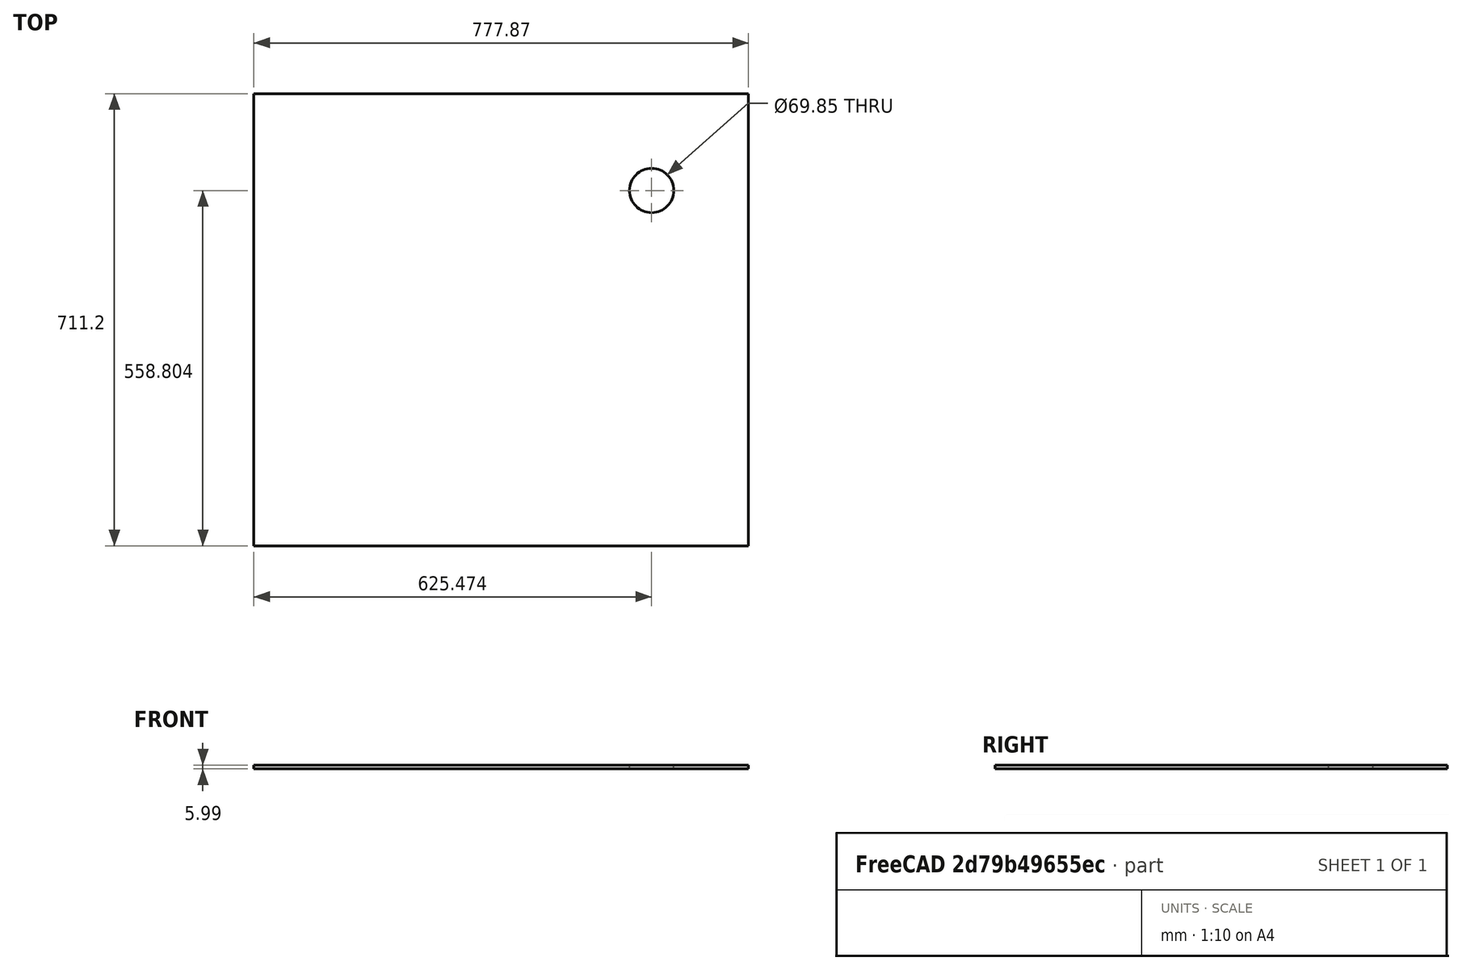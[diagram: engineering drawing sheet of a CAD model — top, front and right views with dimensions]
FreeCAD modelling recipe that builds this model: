
FCSTD DOCUMENT  (FreeCAD 0.19R24267 (Git))
Label: Inv1-P2
License: All rights reserved
LicenseURL: http://en.wikipedia.org/wiki/All_rights_reserved
objects: TechDraw::DrawViewDimension×6, TechDraw::DrawProjGroupItem×2, TechDraw::DrawHatch×2, TechDraw::DrawViewAnnotation×2, Sketcher::SketchObject×1, Part::Extrusion×1, TechDraw::DrawSVGTemplate×1, TechDraw::DrawProjGroup×1, TechDraw::DrawPage×1
note: 2 computed .brp shape members not serialized (recipe doc carries the construction recipe); baked Part::Feature solids carry a one-line shape summary decoded from their .brp

FEATURE [Sketcher::SketchObject] Sketch
  FullyConstrained = false
  sketch-geometry (5):
    g0: LineSegment StartX=-539.321 StartY=433.474 StartZ=0 EndX=238.554 EndY=433.474 EndZ=0
    g1: LineSegment StartX=238.554 StartY=433.474 StartZ=0 EndX=238.554 EndY=-277.726 EndZ=0
    g2: LineSegment StartX=238.554 StartY=-277.726 StartZ=0 EndX=-539.321 EndY=-277.726 EndZ=0
    g3: LineSegment StartX=-539.321 StartY=-277.726 StartZ=0 EndX=-539.321 EndY=433.474 EndZ=0
    g4: Circle CenterX=86.1536 CenterY=281.074 CenterZ=0 NormalX=0 NormalY=0 NormalZ=1 AngleXU=0 Radius=34.925
  constraints (13):
    c: Coincident(g0,g1)
    c: Coincident(g1,g2)
    c: Coincident(g2,g3)
    c: Coincident(g3,g0)
    c: Horizontal(g0)
    c: Horizontal(g2)
    c: Vertical(g1)
    c: Vertical(g3)
    c: DistanceY(g1,g1) = 711.2
    c: DistanceX(g0,g0) = 777.875
    c: Distance(g4,g0) = 152.4
    c: Distance(g4,g1) = 152.4
    c: Diameter(g4) = 69.85
FEATURE [Part::Extrusion] Extrude
  Base = -> Sketch
  Dir = (0,0,1)
  DirMode = 2
  FaceMakerClass = Part::FaceMakerBullseye
  LengthFwd = 5.9944
  LengthRev = 0
  Solid = true
  Symmetric = false
FEATURE [TechDraw::DrawSVGTemplate] Template
  Height = 215.9
  Orientation = 1
  Width = 279.4
FEATURE [TechDraw::DrawProjGroupItem] ProjItem  label="Front"
  CoarseView = false
  Direction = (0,0,1)
  Focus = 100
  HardHidden = false
  IsoCount = 0
  IsoHidden = false
  IsoVisible = false
  LockPosition = true
  Perspective = false
  Rotation = 0
  RotationVector = (1,0,0)
  Scale = 0.2
  ScaleType = 2
  SeamHidden = false
  SeamVisible = true
  SmoothHidden = false
  SmoothVisible = true
  Source = -> [Extrude]
  Type = 0
  X = 0
  XDirection = (1,0,0)
  Y = 0
FEATURE [TechDraw::DrawProjGroupItem] ProjItem001  label="Left"
  CoarseView = false
  Direction = (-1,0,1e-16)
  Focus = 100
  HardHidden = false
  IsoCount = 0
  IsoHidden = false
  IsoVisible = false
  LockPosition = false
  Perspective = false
  Rotation = 0
  RotationVector = (1,0,0)
  Scale = 0.2
  ScaleType = 2
  SeamHidden = false
  SeamVisible = true
  SmoothHidden = false
  SmoothVisible = true
  Source = -> [Extrude]
  Type = 1
  X = 103.584
  XDirection = (1e-16,0,1)
  Y = 0
FEATURE [TechDraw::DrawProjGroup] ProjGroup
  Anchor = -> ProjItem
  AutoDistribute = true
  LockPosition = false
  ProjectionType = 0
  Rotation = 0
  Scale = 0.2
  ScaleType = 2
  Source = -> [Extrude]
  Views = -> [ProjItem,ProjItem001]
  X = 139.7
  Y = 107.95
  spacingX = 15.0114
  spacingY = 15.0114
FEATURE [TechDraw::DrawHatch] Hatch  label="HatchF0"
  HatchPattern = <path>
  Source = -> ProjItem001 [Face0]
FEATURE [TechDraw::DrawHatch] Hatch001  label="Hatch001F0"
  HatchPattern = <path>
  Source = -> ProjItem [Face0]
FEATURE [TechDraw::DrawViewDimension] Dimension
  Arbitrary = false
  ArbitraryTolerances = false
  EqualTolerance = true
  FormatSpec = %.3f
  FormatSpecOverTolerance = %+.3f
  FormatSpecUnderTolerance = %+.3f
  Inverted = false
  LockPosition = false
  MeasureType = 1
  OverTolerance = 0
  References2D = -> [ProjItem]
  Rotation = 0
  ScaleType = 0
  TheoreticalExact = false
  Type = 1
  UnderTolerance = 0
  X = 0
  Y = -75.9014
FEATURE [TechDraw::DrawViewDimension] Dimension001
  Arbitrary = false
  ArbitraryTolerances = false
  EqualTolerance = true
  FormatSpec = %.3f
  FormatSpecOverTolerance = %+.3f
  FormatSpecUnderTolerance = %+.3f
  Inverted = false
  LockPosition = false
  MeasureType = 1
  OverTolerance = 0
  References2D = -> [ProjItem]
  Rotation = 0
  ScaleType = 0
  TheoreticalExact = false
  Type = 2
  UnderTolerance = 0
  X = 82.8238
  Y = 0
FEATURE [TechDraw::DrawViewDimension] Dimension002
  Arbitrary = false
  ArbitraryTolerances = false
  EqualTolerance = true
  FormatSpec = %.3f
  FormatSpecOverTolerance = %+.3f
  FormatSpecUnderTolerance = %+.3f
  Inverted = false
  LockPosition = false
  MeasureType = 1
  OverTolerance = 0
  References2D = -> [ProjItem001]
  Rotation = 0
  ScaleType = 0
  TheoreticalExact = false
  Type = 1
  UnderTolerance = 0
  X = 18.9749
  Y = 68.3089
FEATURE [TechDraw::DrawViewDimension] Dimension003
  Arbitrary = false
  ArbitraryTolerances = false
  EqualTolerance = true
  FormatSpec = ⌀%.3f
  FormatSpecOverTolerance = %+.3f
  FormatSpecUnderTolerance = %+.3f
  Inverted = false
  LockPosition = false
  MeasureType = 1
  OverTolerance = 0
  References2D = -> [ProjItem]
  Rotation = 0
  ScaleType = 0
  TheoreticalExact = false
  Type = 5
  UnderTolerance = 0
  X = 18.305
  Y = 22.7748
FEATURE [TechDraw::DrawViewDimension] Dimension004
  Arbitrary = false
  ArbitraryTolerances = false
  EqualTolerance = true
  FormatSpec = %.3f
  FormatSpecOverTolerance = %+.3f
  FormatSpecUnderTolerance = %+.3f
  Inverted = false
  LockPosition = false
  MeasureType = 1
  OverTolerance = 0
  References2D = -> [ProjItem]
  Rotation = 0
  ScaleType = 0
  TheoreticalExact = false
  Type = 1
  UnderTolerance = 0
  X = 63.1097
  Y = 26.5845
FEATURE [TechDraw::DrawViewDimension] Dimension005
  Arbitrary = false
  ArbitraryTolerances = false
  EqualTolerance = true
  FormatSpec = %.3f
  FormatSpecOverTolerance = %+.3f
  FormatSpecUnderTolerance = %+.3f
  Inverted = false
  LockPosition = false
  MeasureType = 1
  OverTolerance = 0
  References2D = -> [ProjItem]
  Rotation = 0
  ScaleType = 0
  TheoreticalExact = false
  Type = 2
  UnderTolerance = 0
  X = 25.0126
  Y = 55.1409
FEATURE [TechDraw::DrawViewAnnotation] Annotation
  Font = osifont
  LineSpace = 80
  LockPosition = false
  MaxWidth = -1
  Rotation = 0
  ScaleType = 0
  Text = Figure S1 (Inverted 1)  | Panel 2 [right  side exterior baffle] | Quantity: 1
  TextSize = 5.0038
  TextStyle = 0
  X = 47.0369
  Y = 195.58
FEATURE [TechDraw::DrawViewAnnotation] Annotation002
  Font = osifont
  LineSpace = 80
  LockPosition = false
  MaxWidth = -1
  Rotation = 0
  ScaleType = 0
  Text = Units: Inches
  TextSize = 5.0038
  TextStyle = 0
  X = 259.08
  Y = 5.08
FEATURE [TechDraw::DrawPage] Page
  KeepUpdated = true
  NextBalloonIndex = 1
  ProjectionType = 0
  Template = -> Template
  Views = -> [ProjGroup,Dimension,Dimension001,Dimension002,Dimension003,Dimension004,Dimension005,Annotation,Annotation002]
note: 2 file-system paths scrubbed to <path> (originals preserved in the JSON sidecar)
